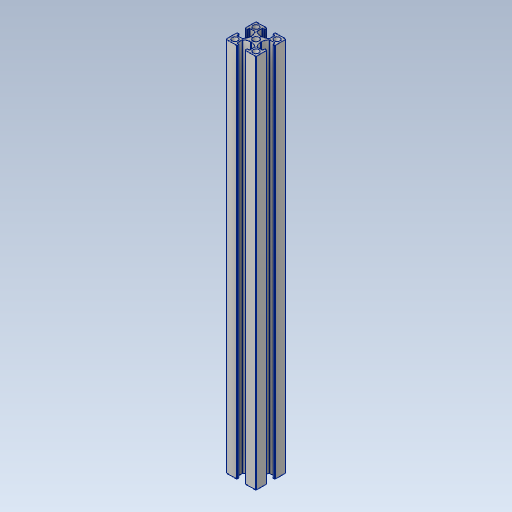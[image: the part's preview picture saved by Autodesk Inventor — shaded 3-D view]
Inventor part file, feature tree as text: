
AUTODESK INVENTOR PART (.ipt)
format: ipt  version: 2021 (Build 250183000, 183)  size: 212,992 bytes
history: native  units: mm
features: other x3, extrude x1
ambient origin geometry x8: Origin, YZ Plane, XZ Plane, XY Plane, X Axis, Y Axis, Z Axis, Center Point
bodies: Body1 (feature_tree)
feature tree (4):
  other  "솔리드1"
  other  "df_2020.dwg"
  extrude  "300mm 2020"  Depth=250.0mm TaperAngle=0.0deg
  other  "2020_Base"
